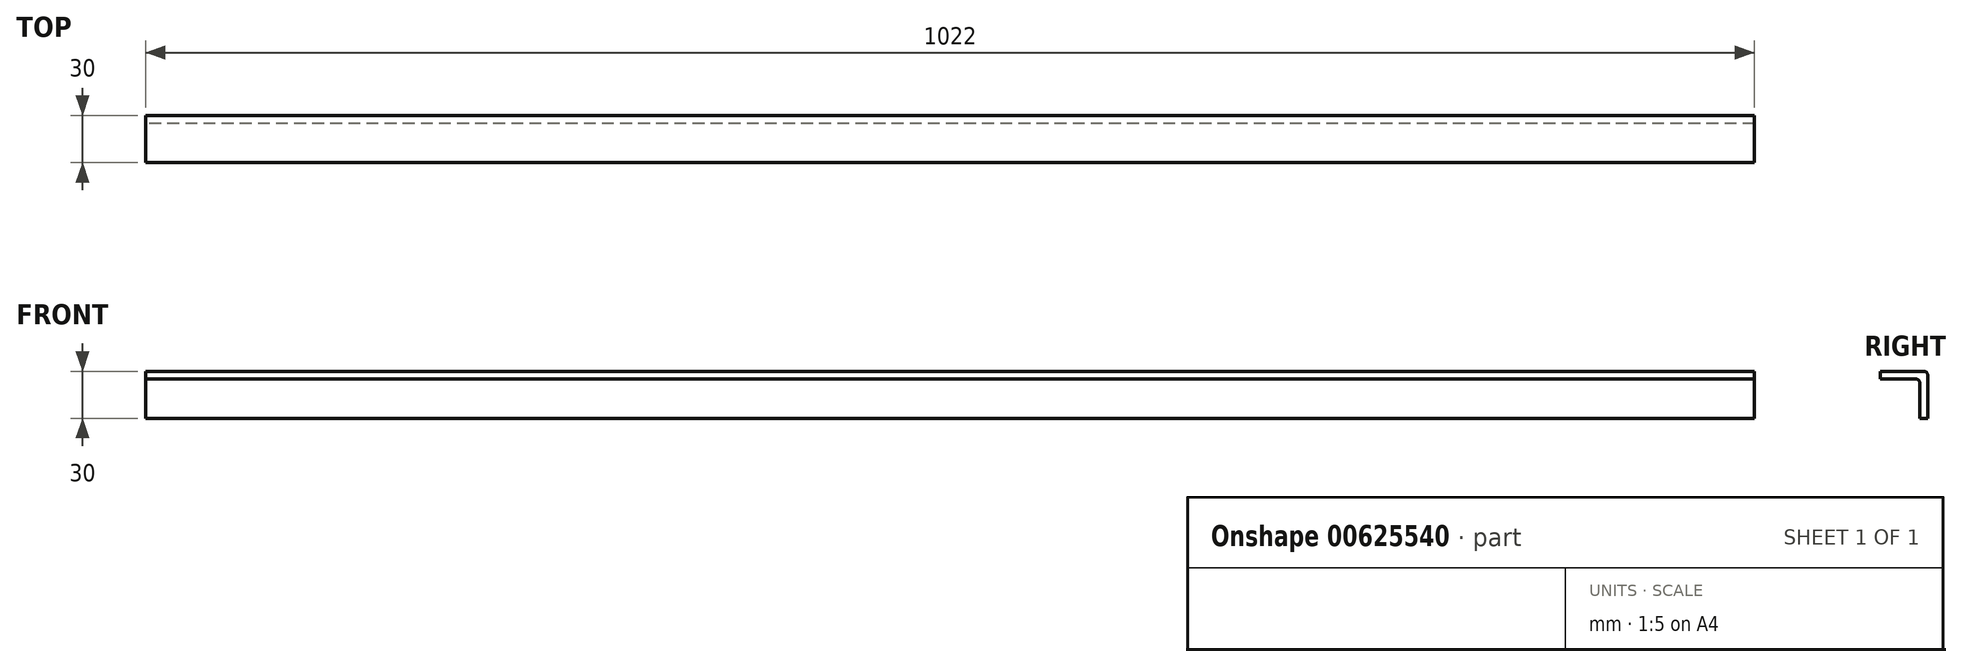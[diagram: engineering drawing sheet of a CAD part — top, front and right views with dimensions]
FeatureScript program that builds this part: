
annotation { "Feature Type Name" : "Feature", "Feature Type Description" : "" }
export const myFeature = defineFeature(function(context is Context, id is Id, definition is map)
    precondition{}
    {
        {
            var Q0;
            Q0=qCreatedBy(makeId("Right.planeOp"),FACE);
            var sketch = newSketch(context, id + "F0", { "sketchPlane" : qUnion([Q0])});
            skLineSegment(sketch, "E0.bottom", {"start": v(12.5, 15) * mm, "end": v(-15, 15) * mm});
            skLineSegment(sketch, "E0.top", {"start": v(15, -15) * mm, "end": v(10, -15) * mm});
            skLineSegment(sketch, "E0.left", {"start": v(15, 12.5) * mm, "end": v(15, -15) * mm});
            skLineSegment(sketch, "E0.right", {"start": v(-15, 15) * mm, "end": v(-15, 10) * mm});
            skPoint(sketch, "E0.middle", {"position": v(0, 0) * mm});
            skLineSegment(sketch, "E1", {"start": v(-15, 10) * mm, "end": v(7.5, 10) * mm});
            skLineSegment(sketch, "E2", {"start": v(10, 7.5) * mm, "end": v(10, -15) * mm});
            skPoint(sketch, "E3.visualSharp", {"position": v(10, 10) * mm});
            skArc(sketch, "E3.filletArc", {"start": v(10, 7.5) * mm, "mid": v(9.27, 9.27) * mm, "end": v(7.5, 10) * mm});
            skPoint(sketch, "E4.visualSharp", {"position": v(15, 15) * mm});
            skArc(sketch, "E4.filletArc", {"start": v(15, 12.5) * mm, "mid": v(14.27, 14.27) * mm, "end": v(12.5, 15) * mm});
            skPoint(sketch, "E5.orphan", {"position": v(-15, -15) * mm});
            skSolve(sketch);
        }
        {
            var Q0;
            Q0 = qSketchRegion(id + "F0", true);
            extrude(context, id + "F1", {"entities" : qUnion([Q0]), "depth" : 1022 * mm, "offsetDistance" : 25 * mm});
        }
    });
